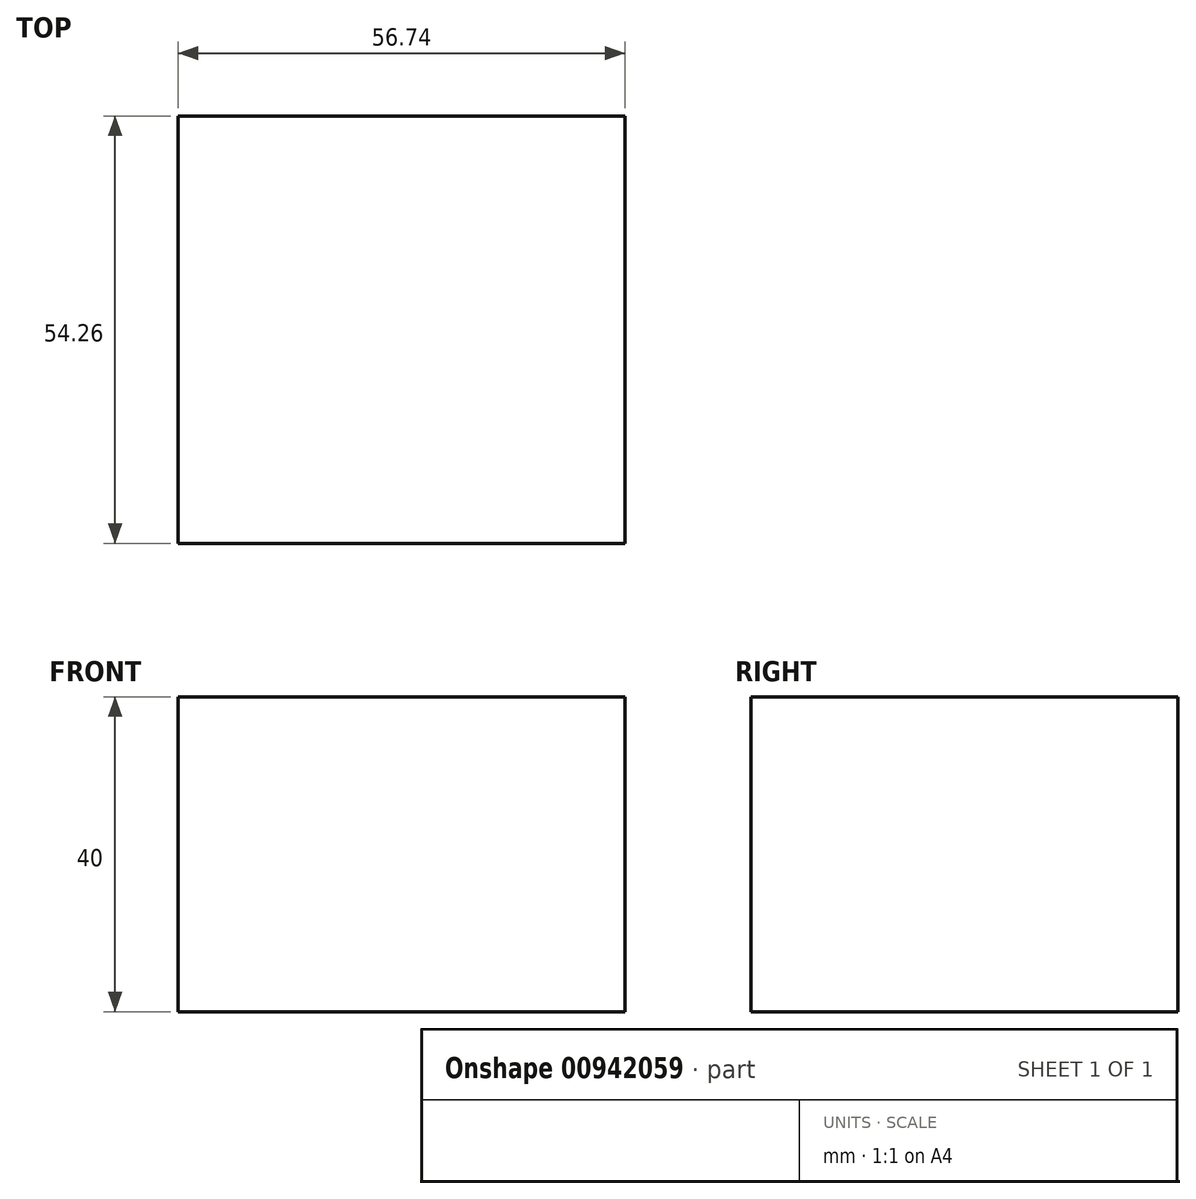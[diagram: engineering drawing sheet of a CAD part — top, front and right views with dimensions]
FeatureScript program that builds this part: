
annotation { "Feature Type Name" : "Feature", "Feature Type Description" : "" }
export const myFeature = defineFeature(function(context is Context, id is Id, definition is map)
    precondition{}
    {
        {
            var Q0;
            Q0=qCreatedBy(makeId("Top.planeOp"),FACE);
            var sketch = newSketch(context, id + "F0", { "sketchPlane" : qUnion([Q0])});
            skLineSegment(sketch, "E0.bottom", {"start": v(-28.37, -27.13) * mm, "end": v(28.37, -27.13) * mm});
            skLineSegment(sketch, "E0.top", {"start": v(-28.37, 27.13) * mm, "end": v(28.37, 27.13) * mm});
            skLineSegment(sketch, "E0.left", {"start": v(-28.37, -27.13) * mm, "end": v(-28.37, 27.13) * mm});
            skLineSegment(sketch, "E0.right", {"start": v(28.37, -27.13) * mm, "end": v(28.37, 27.13) * mm});
            skPoint(sketch, "E0.middle", {"position": v(0, 0) * mm});
            skSolve(sketch);
        }
        {
            var Q0;
            Q0 = qSketchRegion(id + "F0", true);
            extrude(context, id + "F1", {"entities" : qUnion([Q0]), "depth" : 40 * mm, "offsetDistance" : 25.4 * mm});
        }
        {
            var Q0;
            Q0=qCreatedBy(makeId("Top.planeOp"),FACE);
            var sketch = newSketch(context, id + "F2", { "sketchPlane" : qUnion([Q0])});
            skFitSpline(sketch, "E1", {"points": [v(-29.74, 0) * mm, v(-45.6, 9.91) * mm, v(-27.76, 28) * mm, v(0, 47.6) * mm, v(29.02, 27.02) * mm, v(56.04, 0) * mm, v(29.26, -27.53) * mm, v(29.26, -27.03) * mm, v(0, -47.6) * mm, v(-27.76, -27.53) * mm, v(-55.77, -20.58) * mm, v(-29.74, 0) * mm]});
            skSolve(sketch);
        }
        {
            var Q0;
            Q0=sQuery(id+"F2.wireOp",EDGE,"E1");
            extrude(context, id + "F3", {"bodyType" : ToolBodyType.SURFACE, "surfaceEntities" : qUnion([Q0]), "depth" : 25.4 * mm, "offsetDistance" : 25.4 * mm});
        }
    });
